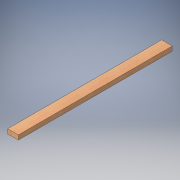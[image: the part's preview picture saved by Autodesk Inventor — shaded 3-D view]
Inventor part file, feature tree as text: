
AUTODESK INVENTOR PART (.ipt)
format: ipt  version: 2016 (Build 200138000, 138)  size: 97,280 bytes
history: native  units: in
note: dims shown in document units (in); Inventor stores cm internally (conversion verified against a paired STEP export)
features: extrude x1, sketch x1
ambient origin geometry x8: Origin, YZ Plane, XZ Plane, XY Plane, X Axis, Y Axis, Z Axis, Center Point
bodies: Solid1 (feature_tree)
feature tree (2):
  extrude  "Extrusion1"  Depth=1.5in
  sketch  "Sketch1"  dims[d0=3.5in d1=1.5in d2=50.75in d3=0.0in]
